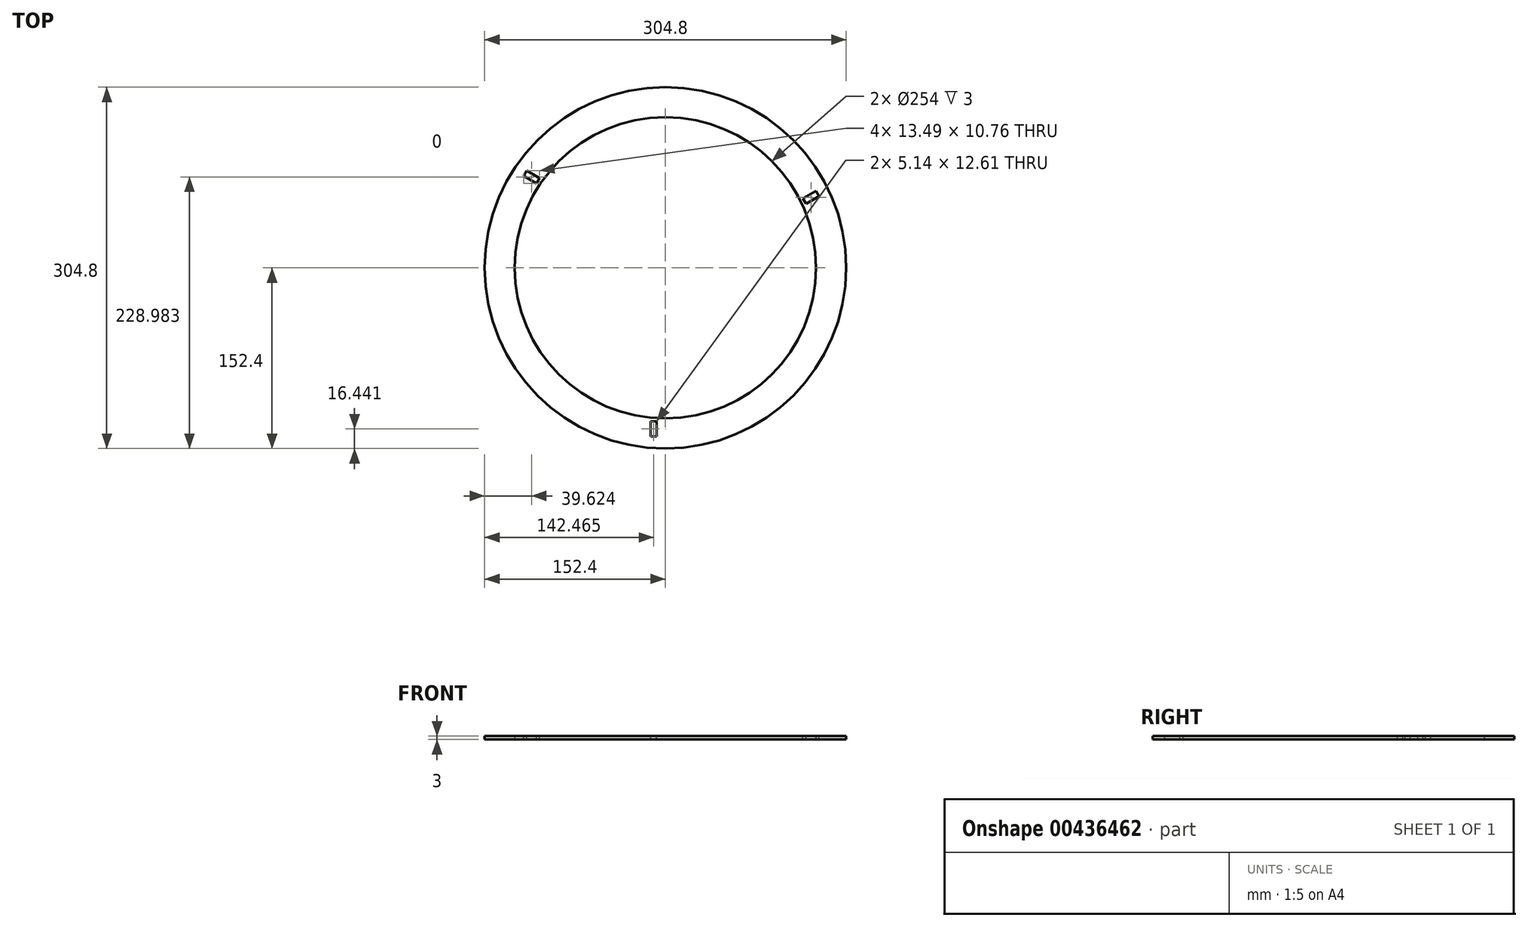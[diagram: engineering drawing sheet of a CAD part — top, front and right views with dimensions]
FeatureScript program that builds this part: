
annotation { "Feature Type Name" : "Feature", "Feature Type Description" : "" }
export const myFeature = defineFeature(function(context is Context, id is Id, definition is map)
    precondition{}
    {
        {
            var Q0;
            Q0=qCreatedBy(makeId("Top.planeOp"),FACE);
            var sketch = newSketch(context, id + "F0", { "sketchPlane" : qUnion([Q0])});
            skCircle(sketch, "E0", {"center": v(0, 0) * mm, "radius": 152.4 * mm});
            skCircle(sketch, "E1", {"center": v(0, 0) * mm, "radius": 127 * mm});
            skSolve(sketch);
        }
        {
            var Q0;
            Q0=makeQuery(id+"F0.imprint","IMPRINT",FACE,{"disambiguationData":[TD([[makeQuery(id+"F0.imprint","IMPRINT",EDGE,{"derivedFrom":sQuery(id+"F0.wireOp",EDGE,"E0")}),1.0]])]});
            extrude(context, id + "F1", {"entities" : qUnion([Q0]), "depth" : 3 * mm});
        }
        {
            var Q0;
            Q0=makeQuery(id+"F1.opExtrude","CAP_FACE",FACE,{"disambiguationData":[OSD([sQuery(id+"F0.wireOp",EDGE,"E0"),sQuery(id+"F0.wireOp",EDGE,"E1")])],"isStart":false});
            var sketch = newSketch(context, id + "F2", { "sketchPlane" : qUnion([Q0])});
            skLineSegment(sketch, "E2.bottom", {"start": v(-7.37, -142.27) * mm, "end": v(-12.5, -142.27) * mm});
            skLineSegment(sketch, "E2.top", {"start": v(-7.37, -129.65) * mm, "end": v(-12.5, -129.65) * mm});
            skLineSegment(sketch, "E2.left", {"start": v(-7.37, -142.27) * mm, "end": v(-7.37, -129.65) * mm});
            skLineSegment(sketch, "E2.right", {"start": v(-12.5, -142.27) * mm, "end": v(-12.5, -129.65) * mm});
            skLineSegment(sketch, "E3.1.0", {"start": v(129.46, 60.3) * mm, "end": v(118.53, 54) * mm});
            skLineSegment(sketch, "E3.1.1", {"start": v(126.89, 64.75) * mm, "end": v(115.96, 58.45) * mm});
            skLineSegment(sketch, "E3.1.2", {"start": v(115.96, 58.45) * mm, "end": v(118.53, 54) * mm});
            skLineSegment(sketch, "E3.1.3", {"start": v(126.89, 64.75) * mm, "end": v(129.46, 60.3) * mm});
            skLineSegment(sketch, "E3.2.0", {"start": v(-116.95, 81.96) * mm, "end": v(-106.03, 75.65) * mm});
            skLineSegment(sketch, "E3.2.1", {"start": v(-119.52, 77.51) * mm, "end": v(-108.6, 71.2) * mm});
            skLineSegment(sketch, "E3.2.2", {"start": v(-108.6, 71.2) * mm, "end": v(-106.03, 75.65) * mm});
            skLineSegment(sketch, "E3.2.3", {"start": v(-119.52, 77.51) * mm, "end": v(-116.95, 81.96) * mm});
            skPoint(sketch, "E3.center", {"position": v(0, 0) * mm});
            skSolve(sketch);
        }
        {
            var Q0;
            Q0=makeQuery(id+"F2.imprint","IMPRINT",FACE,{"disambiguationData":[TD([[makeQuery(id+"F2.imprint","IMPRINT",EDGE,{"derivedFrom":sQuery(id+"F2.wireOp",EDGE,"E3.2.0")}),-1.0]])]});
            var Q1;
            Q1=makeQuery(id+"F2.imprint","IMPRINT",FACE,{"disambiguationData":[TD([[makeQuery(id+"F2.imprint","IMPRINT",EDGE,{"derivedFrom":sQuery(id+"F2.wireOp",EDGE,"E3.1.0")}),-1.0]])]});
            var Q2;
            Q2=makeQuery(id+"F2.imprint","IMPRINT",FACE,{"disambiguationData":[TD([[makeQuery(id+"F2.imprint","IMPRINT",EDGE,{"derivedFrom":sQuery(id+"F2.wireOp",EDGE,"E2.bottom")}),-1.0]])]});
            extrude(context, id + "F3", {"entities" : qUnion([Q0, Q1, Q2]), "operationType" : NewBodyOperationType.REMOVE, "oppositeDirection" : true, "depth" : 25.4 * mm, "offsetDistance" : 25.4 * mm});
        }
    });
